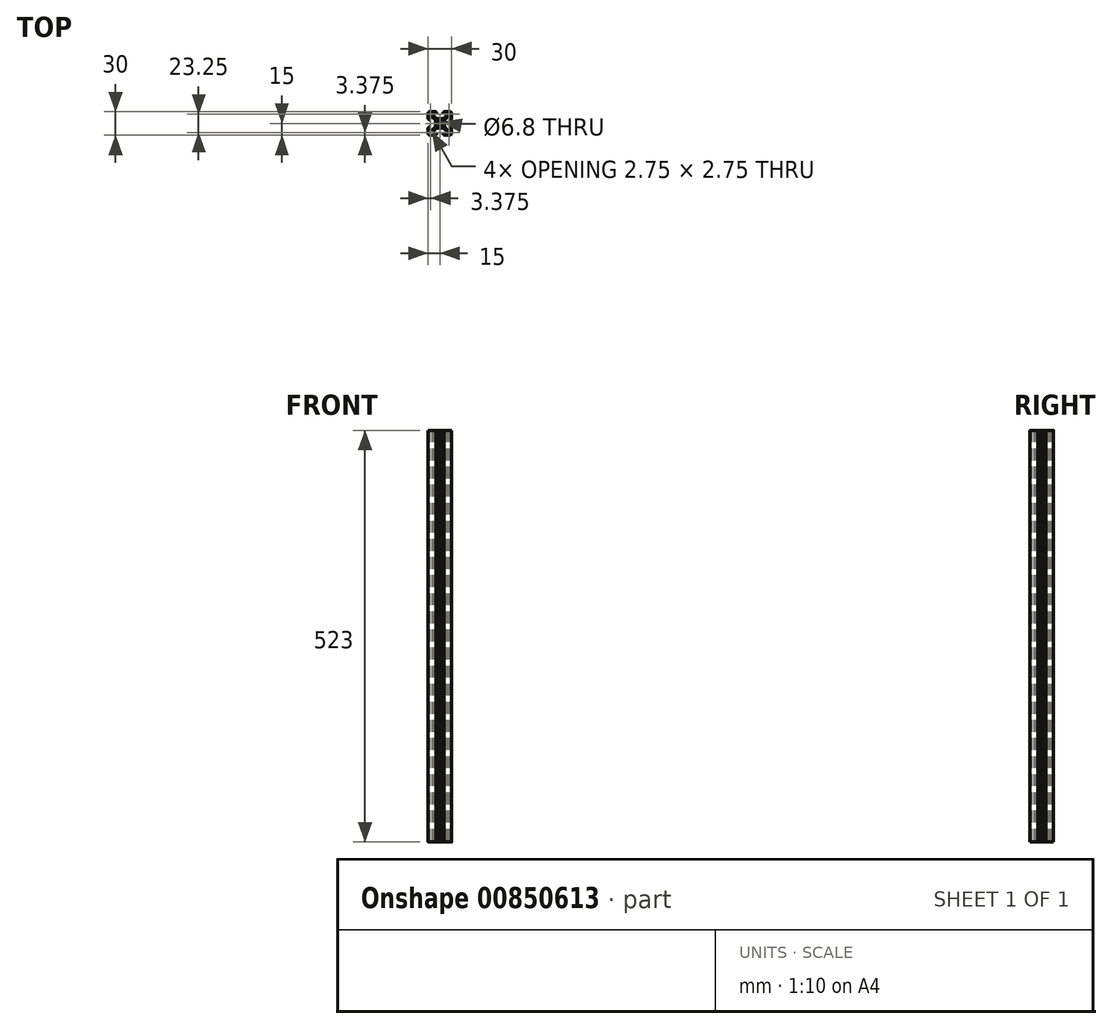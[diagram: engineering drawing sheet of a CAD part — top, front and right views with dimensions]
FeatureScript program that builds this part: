
annotation { "Feature Type Name" : "Feature", "Feature Type Description" : "" }
export const myFeature = defineFeature(function(context is Context, id is Id, definition is map)
    precondition{}
    {
        {
            var Q0;
            Q0=qCreatedBy(makeId("Top.planeOp"),FACE);
            var sketch = newSketch(context, id + "F0", { "sketchPlane" : qUnion([Q0])});
            skLineSegment(sketch, "E0", {"start": v(-5.1, 15) * mm, "end": v(-5.1, 14) * mm});
            skLineSegment(sketch, "E1", {"start": v(-5.1, 14) * mm, "end": v(-4.1, 14) * mm});
            skLineSegment(sketch, "E2", {"start": v(-4.1, 14) * mm, "end": v(-4.1, 13) * mm});
            skLineSegment(sketch, "E3", {"start": v(-4.1, 13) * mm, "end": v(-8.25, 13) * mm});
            skLineSegment(sketch, "E4", {"start": v(-5.1, 15) * mm, "end": v(-12.5, 15) * mm});
            skArc(sketch, "E5", {"start": v(-12.5, 15) * mm, "mid": v(-14.27, 14.27) * mm, "end": v(-15, 12.5) * mm});
            skLineSegment(sketch, "E6", {"start": v(-15, 12.5) * mm, "end": v(-15, 5.1) * mm});
            skLineSegment(sketch, "E7", {"start": v(-15, 5.1) * mm, "end": v(-14, 5.1) * mm});
            skLineSegment(sketch, "E8", {"start": v(-14, 5.1) * mm, "end": v(-14, 4.1) * mm});
            skLineSegment(sketch, "E9", {"start": v(-14, 4.1) * mm, "end": v(-13, 4.1) * mm});
            skLineSegment(sketch, "E10", {"start": v(-13, 4.1) * mm, "end": v(-13, 8.25) * mm});
            skArc(sketch, "E11", {"start": v(-3.4, 0) * mm, "mid": v(-2.4, 2.4) * mm, "end": v(0, 3.4) * mm});
            skLineSegment(sketch, "E12", {"start": v(-5.5, 0) * mm, "end": v(-3.4, 0) * mm});
            skLineSegment(sketch, "E13", {"start": v(0, 3.4) * mm, "end": v(0, 5.5) * mm});
            skLineSegment(sketch, "E14", {"start": v(-8.25, 13) * mm, "end": v(-8.25, 9.7) * mm});
            skLineSegment(sketch, "E15", {"start": v(-8.25, 9.7) * mm, "end": v(-4.35, 5.8) * mm});
            skLineSegment(sketch, "E16", {"start": v(-4.35, 5.8) * mm, "end": v(-0.5, 5.8) * mm});
            skLineSegment(sketch, "E17", {"start": v(-0.5, 5.8) * mm, "end": v(0, 5.5) * mm});
            skLineSegment(sketch, "E18", {"start": v(-5.5, 0) * mm, "end": v(-5.8, 0.5) * mm});
            skLineSegment(sketch, "E19", {"start": v(-5.8, 0.5) * mm, "end": v(-5.8, 4.35) * mm});
            skLineSegment(sketch, "E20", {"start": v(-5.8, 4.35) * mm, "end": v(-9.7, 8.25) * mm});
            skLineSegment(sketch, "E21", {"start": v(-9.7, 8.25) * mm, "end": v(-13, 8.25) * mm});
            skLineSegment(sketch, "E22", {"start": v(-12.5, 13) * mm, "end": v(-10.75, 13) * mm});
            skArc(sketch, "E23", {"start": v(-10.75, 13) * mm, "mid": v(-10.4, 12.85) * mm, "end": v(-10.25, 12.5) * mm});
            skLineSegment(sketch, "E24", {"start": v(-10.25, 12.5) * mm, "end": v(-10.25, 10.75) * mm});
            skArc(sketch, "E25", {"start": v(-10.25, 10.75) * mm, "mid": v(-10.4, 10.4) * mm, "end": v(-10.75, 10.25) * mm});
            skLineSegment(sketch, "E26", {"start": v(-10.75, 10.25) * mm, "end": v(-12.5, 10.25) * mm});
            skArc(sketch, "E27", {"start": v(-12.5, 10.25) * mm, "mid": v(-12.85, 10.4) * mm, "end": v(-13, 10.75) * mm});
            skLineSegment(sketch, "E28", {"start": v(-13, 10.75) * mm, "end": v(-13, 12.5) * mm});
            skArc(sketch, "E29", {"start": v(-13, 12.5) * mm, "mid": v(-12.85, 12.85) * mm, "end": v(-12.5, 13) * mm});
            skSolve(sketch);
        }
        {
            var Q0;
            Q0 = qSketchRegion(id + "F0", true);
            extrude(context, id + "F1", {"entities" : qUnion([Q0]), "endBound" : BoundingType.SYMMETRIC, "depth" : 523 * mm, "offsetDistance" : 25 * mm});
        }
        {
            var Q0;
            Q0=makeQuery(id+"F1.opExtrude","SWEPT_BODY",BODY,{"disambiguationData":[OSD([sQuery(id+"F0.wireOp",EDGE,"E0"),sQuery(id+"F0.wireOp",EDGE,"E1"),sQuery(id+"F0.wireOp",EDGE,"E2"),sQuery(id+"F0.wireOp",EDGE,"E3"),sQuery(id+"F0.wireOp",EDGE,"E4"),sQuery(id+"F0.wireOp",EDGE,"E5"),sQuery(id+"F0.wireOp",EDGE,"E6"),sQuery(id+"F0.wireOp",EDGE,"E7"),sQuery(id+"F0.wireOp",EDGE,"E8"),sQuery(id+"F0.wireOp",EDGE,"E9"),sQuery(id+"F0.wireOp",EDGE,"E10"),sQuery(id+"F0.wireOp",EDGE,"E11"),sQuery(id+"F0.wireOp",EDGE,"E12"),sQuery(id+"F0.wireOp",EDGE,"E13"),sQuery(id+"F0.wireOp",EDGE,"E14"),sQuery(id+"F0.wireOp",EDGE,"E15"),sQuery(id+"F0.wireOp",EDGE,"E16"),sQuery(id+"F0.wireOp",EDGE,"E17"),sQuery(id+"F0.wireOp",EDGE,"E18"),sQuery(id+"F0.wireOp",EDGE,"E19"),sQuery(id+"F0.wireOp",EDGE,"E20"),sQuery(id+"F0.wireOp",EDGE,"E21"),sQuery(id+"F0.wireOp",EDGE,"E22"),sQuery(id+"F0.wireOp",EDGE,"E23"),sQuery(id+"F0.wireOp",EDGE,"E24"),sQuery(id+"F0.wireOp",EDGE,"E25"),sQuery(id+"F0.wireOp",EDGE,"E26"),sQuery(id+"F0.wireOp",EDGE,"E27"),sQuery(id+"F0.wireOp",EDGE,"E28"),sQuery(id+"F0.wireOp",EDGE,"E29")])]});
            var Q1;
            Q1=makeQuery(id+"F1.opExtrude","SWEPT_FACE",FACE,{"disambiguationData":[OSD([sQuery(id+"F0.wireOp",EDGE,"E13")])]});
            mirror(context, id + "F2", {"operationType" : NewBodyOperationType.ADD, "entities" : qUnion([Q0]), "mirrorPlane" : qUnion([Q1])});
        }
        {
            var Q0;
            Q0=makeQuery(id+"F1.opExtrude","SWEPT_BODY",BODY,{"disambiguationData":[OSD([sQuery(id+"F0.wireOp",EDGE,"E0"),sQuery(id+"F0.wireOp",EDGE,"E1"),sQuery(id+"F0.wireOp",EDGE,"E2"),sQuery(id+"F0.wireOp",EDGE,"E3"),sQuery(id+"F0.wireOp",EDGE,"E4"),sQuery(id+"F0.wireOp",EDGE,"E5"),sQuery(id+"F0.wireOp",EDGE,"E6"),sQuery(id+"F0.wireOp",EDGE,"E7"),sQuery(id+"F0.wireOp",EDGE,"E8"),sQuery(id+"F0.wireOp",EDGE,"E9"),sQuery(id+"F0.wireOp",EDGE,"E10"),sQuery(id+"F0.wireOp",EDGE,"E11"),sQuery(id+"F0.wireOp",EDGE,"E12"),sQuery(id+"F0.wireOp",EDGE,"E13"),sQuery(id+"F0.wireOp",EDGE,"E14"),sQuery(id+"F0.wireOp",EDGE,"E15"),sQuery(id+"F0.wireOp",EDGE,"E16"),sQuery(id+"F0.wireOp",EDGE,"E17"),sQuery(id+"F0.wireOp",EDGE,"E18"),sQuery(id+"F0.wireOp",EDGE,"E19"),sQuery(id+"F0.wireOp",EDGE,"E20"),sQuery(id+"F0.wireOp",EDGE,"E21"),sQuery(id+"F0.wireOp",EDGE,"E22"),sQuery(id+"F0.wireOp",EDGE,"E23"),sQuery(id+"F0.wireOp",EDGE,"E24"),sQuery(id+"F0.wireOp",EDGE,"E25"),sQuery(id+"F0.wireOp",EDGE,"E26"),sQuery(id+"F0.wireOp",EDGE,"E27"),sQuery(id+"F0.wireOp",EDGE,"E28"),sQuery(id+"F0.wireOp",EDGE,"E29")])]});
            var Q1;
            Q1=makeQuery(id+"F1.opExtrude","SWEPT_FACE",FACE,{"disambiguationData":[OSD([sQuery(id+"F0.wireOp",EDGE,"E12")])]});
            mirror(context, id + "F3", {"operationType" : NewBodyOperationType.ADD, "entities" : qUnion([Q0]), "mirrorPlane" : qUnion([Q1])});
        }
    });
